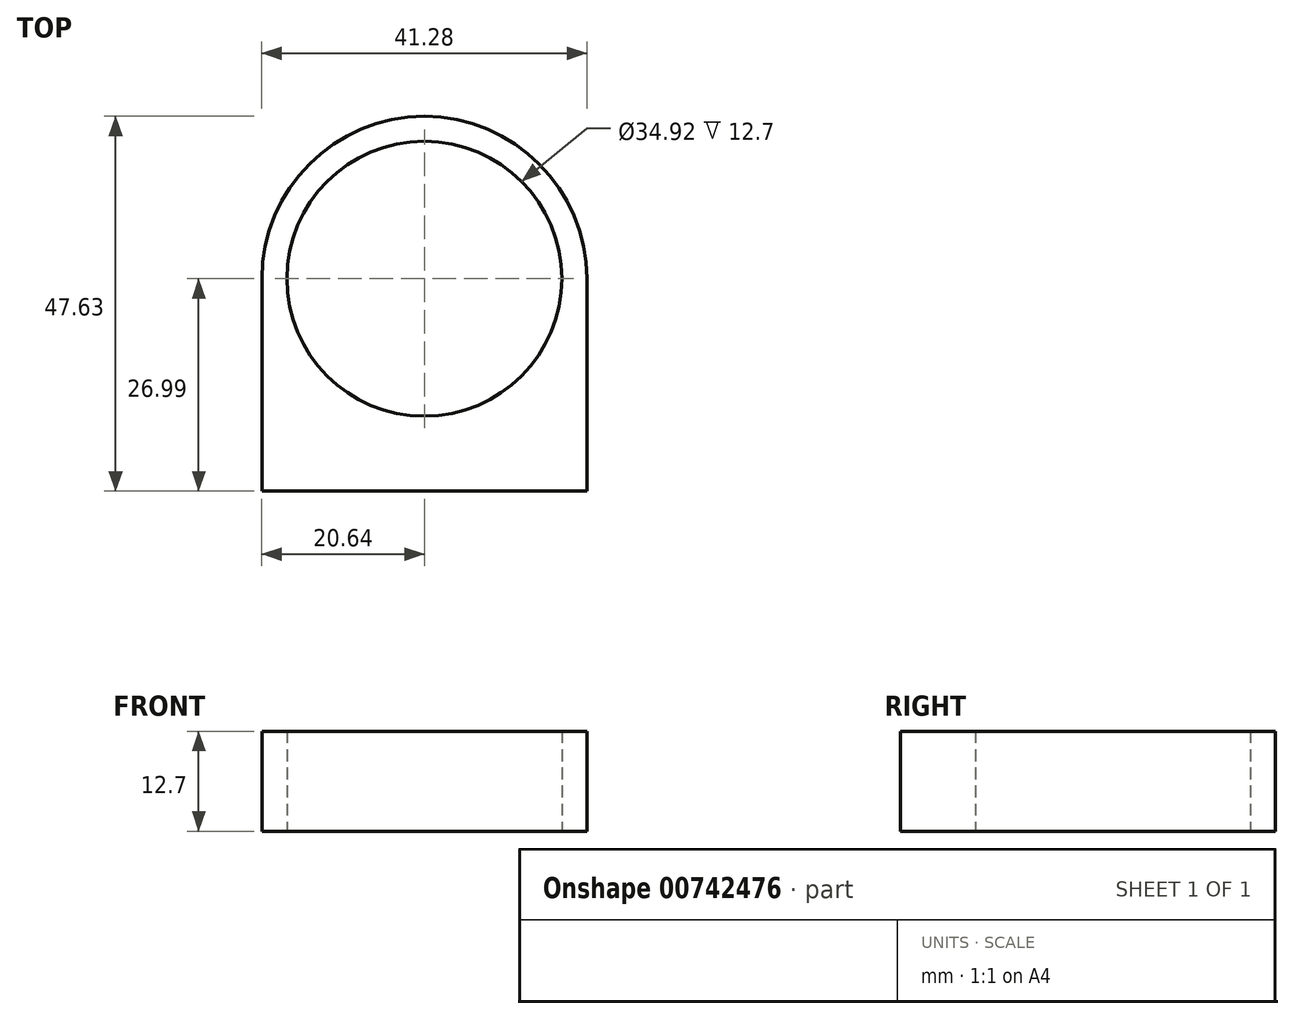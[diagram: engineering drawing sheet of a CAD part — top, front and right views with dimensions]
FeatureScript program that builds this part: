
annotation { "Feature Type Name" : "Feature", "Feature Type Description" : "" }
export const myFeature = defineFeature(function(context is Context, id is Id, definition is map)
    precondition{}
    {
        {
            var Q0;
            Q0=qCreatedBy(makeId("Top.planeOp"),FACE);
            var sketch = newSketch(context, id + "F0", { "sketchPlane" : qUnion([Q0])});
            skCircle(sketch, "E0", {"center": v(0, 0) * mm, "radius": 17.46 * mm});
            skCircle(sketch, "E1.0", {"center": v(0, 0) * mm, "radius": 20.64 * mm});
            skLineSegment(sketch, "E2", {"start": v(-20.64, 0) * mm, "end": v(-20.64, -26.99) * mm});
            skLineSegment(sketch, "E3", {"start": v(-20.64, -26.99) * mm, "end": v(0, -26.99) * mm});
            skLineSegment(sketch, "E4.MirrorCS", {"start": v(20.64, 0) * mm, "end": v(20.64, -26.99) * mm});
            skLineSegment(sketch, "E5.MirrorCS", {"start": v(20.64, -26.99) * mm, "end": v(0, -26.99) * mm});
            skSolve(sketch);
        }
        {
            var Q0;
            Q0 = qSketchRegion(id + "F0", true);
            extrude(context, id + "F1", {"entities" : qUnion([Q0]), "depth" : 12.7 * mm, "offsetDistance" : 25.4 * mm});
        }
    });
